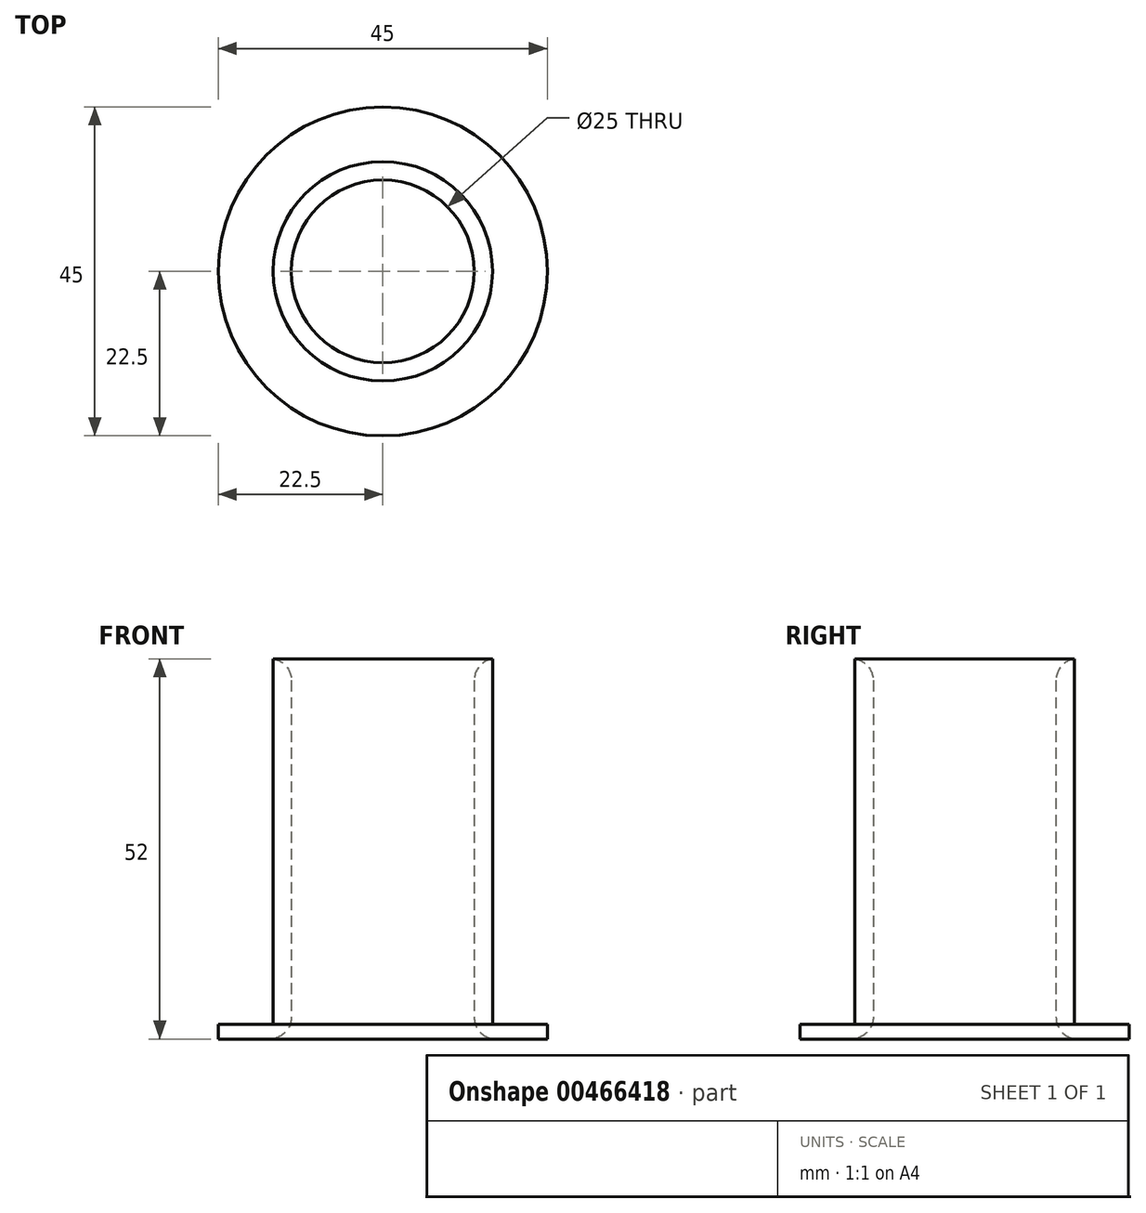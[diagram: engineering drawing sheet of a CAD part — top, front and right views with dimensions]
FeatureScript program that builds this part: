
annotation { "Feature Type Name" : "Feature", "Feature Type Description" : "" }
export const myFeature = defineFeature(function(context is Context, id is Id, definition is map)
    precondition{}
    {
        {
            var Q0;
            Q0=qCreatedBy(makeId("Top.planeOp"),FACE);
            var sketch = newSketch(context, id + "F0", { "sketchPlane" : qUnion([Q0])});
            skCircle(sketch, "E0", {"center": v(0, 0) * mm, "radius": 12.5 * mm});
            skCircle(sketch, "E1", {"center": v(0, 0) * mm, "radius": 22.5 * mm});
            skSolve(sketch);
        }
        {
            var Q0;
            Q0=makeQuery(id+"F0.imprint","IMPRINT",FACE,{"disambiguationData":[TD([[makeQuery(id+"F0.imprint","IMPRINT",EDGE,{"derivedFrom":sQuery(id+"F0.wireOp",EDGE,"E0")}),-1.0]])]});
            extrude(context, id + "F1", {"entities" : qUnion([Q0]), "depth" : 2 * mm, "offsetDistance" : 25 * mm});
        }
        {
            var Q0;
            Q0=makeQuery(id+"F1.opExtrude","CAP_FACE",FACE,{"disambiguationData":[OSD([sQuery(id+"F0.wireOp",EDGE,"E0"),sQuery(id+"F0.wireOp",EDGE,"E1")])],"isStart":false});
            var sketch = newSketch(context, id + "F2", { "sketchPlane" : qUnion([Q0])});
            skCircle(sketch, "E2", {"center": v(0, 0) * mm, "radius": 15 * mm});
            skSolve(sketch);
        }
        {
            var Q0;
            Q0=makeQuery(id+"F2.imprint","IMPRINT",FACE,{"disambiguationData":[TD([[makeQuery(id+"F2.imprint","IMPRINT",EDGE,{"derivedFrom":sQuery(id+"F2.wireOp",EDGE,"E2")}),1.0]])]});
            extrude(context, id + "F3", {"entities" : qUnion([Q0]), "operationType" : NewBodyOperationType.ADD, "depth" : 50 * mm, "offsetDistance" : 25 * mm});
        }
        {
            var Q0;
            Q0=makeQuery(id+"F1.opExtrude","CAP_EDGE",EDGE,{"disambiguationData":[OSD([sQuery(id+"F0.wireOp",EDGE,"E0")])],"isStart":true});
            var Q1;
            Q1=makeQuery(id+"F3.opExtrude","CAP_EDGE",EDGE,{"disambiguationData":[OSD([sQuery(id+"F0.wireOp",EDGE,"E0")])],"isStart":false});
            fillet(context, id + "F4", {"entities" : qUnion([Q0, Q1]), "radius" : 3 * mm, "tangentPropagation" : true, "allowEdgeOverflow" : false});
        }
    });
